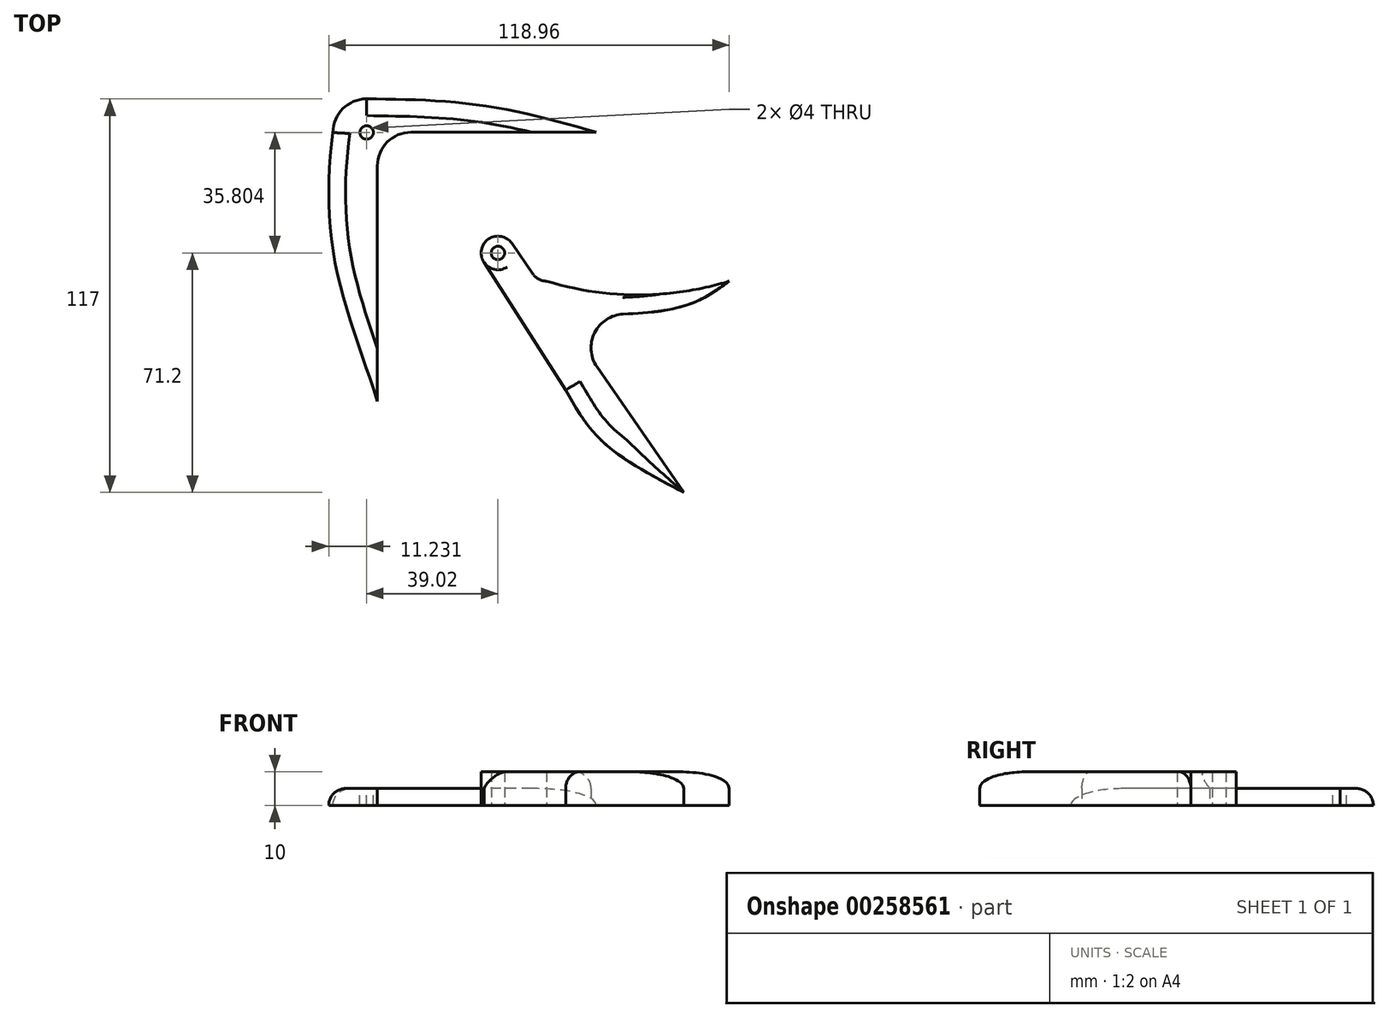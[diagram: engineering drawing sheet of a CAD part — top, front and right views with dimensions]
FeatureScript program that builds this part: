
annotation { "Feature Type Name" : "Feature", "Feature Type Description" : "" }
export const myFeature = defineFeature(function(context is Context, id is Id, definition is map)
    precondition{}
    {
        {
            var Q0;
            Q0=qCreatedBy(makeId("Top.planeOp"),FACE);
            var sketch = newSketch(context, id + "F0", { "sketchPlane" : qUnion([Q0])});
            skLineSegment(sketch, "E0", {"start": v(30.76, 64.9) * mm, "end": v(-24.24, 64.9) * mm});
            skLineSegment(sketch, "E1", {"start": v(-34.24, 54.9) * mm, "end": v(-34.24, -15.1) * mm});
            skPoint(sketch, "E2.visualSharp", {"position": v(-46.55, 74.88) * mm});
            skArc(sketch, "E2.filletArc", {"start": v(-37.45, 74.81) * mm, "mid": v(-44.52, 71.89) * mm, "end": v(-47.45, 64.81) * mm});
            skPoint(sketch, "E3.visualSharp", {"position": v(-34.24, 64.9) * mm});
            skArc(sketch, "E3.filletArc", {"start": v(-24.24, 64.9) * mm, "mid": v(-31.3, 61.96) * mm, "end": v(-34.24, 54.9) * mm});
            skPoint(sketch, "E4.1.internal.snap0", {"position": v(-4.05, 74.88) * mm});
            skFitSpline(sketch, "E4", {"points": [v(-37.45, 74.81) * mm, v(-4.05, 72.97) * mm, v(30.76, 64.9) * mm], "startDerivative": vector(65.7, -0.83) * mm, "endDerivative": vector(64.31, -19.13) * mm});
            skFitSpline(sketch, "E5", {"points": [v(-47.45, 64.81) * mm, v(-46.55, 24.86) * mm, v(-34.24, -15.1) * mm], "startDerivative": vector(-10.85, -80.35) * mm, "endDerivative": vector(24.85, -79.1) * mm});
            skSolve(sketch);
        }
        {
            var Q0;
            Q0=makeQuery(id+"F0.imprint","IMPRINT",FACE,{"disambiguationData":[TD([[makeQuery(id+"F0.imprint","IMPRINT",EDGE,{"derivedFrom":sQuery(id+"F0.wireOp",EDGE,"E0")}),-1.0]])]});
            extrude(context, id + "F1", {"entities" : qUnion([Q0]), "depth" : 5 * mm});
        }
        {
            var Q0;
            Q0=makeQuery(id+"F1.opExtrude","CAP_EDGE",EDGE,{"disambiguationData":[OSD([sQuery(id+"F0.wireOp",EDGE,"E5")])],"isStart":false});
            var Q1;
            Q1=makeQuery(id+"F1.opExtrude","CAP_EDGE",EDGE,{"disambiguationData":[OSD([sQuery(id+"F0.wireOp",EDGE,"E4")])],"isStart":false});
            var Q2;
            Q2=makeQuery(id+"F1.opExtrude","CAP_EDGE",EDGE,{"disambiguationData":[OSD([sQuery(id+"F0.wireOp",EDGE,"E2.filletArc")])],"isStart":false});
            fillet(context, id + "F2", {"entities" : qUnion([Q0, Q1, Q2]), "radius" : 5 * mm, "tangentPropagation" : true, "allowEdgeOverflow" : false});
        }
        {
            var Q0;
            Q0=qCreatedBy(makeId("Top.planeOp"),FACE);
            var sketch = newSketch(context, id + "F3", { "sketchPlane" : qUnion([Q0])});
            skArc(sketch, "E6", {"start": v(5.7, 31.84) * mm, "mid": v(-1.26, 33.13) * mm, "end": v(-2.55, 26.18) * mm});
            skLineSegment(sketch, "E7", {"start": v(-2.55, 26.18) * mm, "end": v(21.67, -11.75) * mm});
            skFitSpline(sketch, "E8", {"points": [v(20.28, 10.63) * mm, v(56.46, 13.13) * mm, v(70.28, 20.63) * mm], "startDerivative": vector(67.6, -0.3) * mm, "endDerivative": vector(29.8, 21.82) * mm});
            skLineSegment(sketch, "E9", {"start": v(5.7, 31.84) * mm, "end": v(11.91, 22.8) * mm});
            skLineSegment(sketch, "E10", {"start": v(30.98, -4.86) * mm, "end": v(56.77, -42.19) * mm});
            skFitSpline(sketch, "E11", {"points": [v(21.67, -11.75) * mm, v(32.7, -27.13) * mm, v(56.77, -42.19) * mm], "startDerivative": vector(20.27, -35.71) * mm, "endDerivative": vector(48.82, -25.74) * mm});
            skArc(sketch, "E12.filletArc", {"start": v(38.8, 10.82) * mm, "mid": v(30.26, 5.29) * mm, "end": v(30.98, -4.86) * mm});
            skPoint(sketch, "E13.visualSharp", {"position": v(13.4, 20.63) * mm});
            skArc(sketch, "E13.filletArc", {"start": v(11.91, 22.8) * mm, "mid": v(13.7, 21.2) * mm, "end": v(16.03, 20.63) * mm});
            skArc(sketch, "E14", {"start": v(16.03, 20.63) * mm, "mid": v(43.16, 16.55) * mm, "end": v(70.28, 20.63) * mm});
            skCircle(sketch, "E15", {"center": v(1.57, 29.01) * mm, "radius": 2 * mm});
            skSolve(sketch);
        }
        {
            var Q0;
            Q0=makeQuery(id+"F3.imprint","IMPRINT",FACE,{"disambiguationData":[TD([[makeQuery(id+"F3.imprint","IMPRINT",EDGE,{"derivedFrom":sQuery(id+"F3.wireOp",EDGE,"E6")}),1.0]])]});
            extrude(context, id + "F4", {"entities" : qUnion([Q0]), "depth" : 10 * mm});
        }
        {
            var Q0;
            Q0=makeQuery(id+"F4.opExtrude","CAP_EDGE",EDGE,{"disambiguationData":[OSD([sQuery(id+"F3.wireOp",EDGE,"E7")])],"isStart":false});
            var Q1;
            Q1=makeQuery(id+"F4.opExtrude","CAP_EDGE",EDGE,{"disambiguationData":[OSD([sQuery(id+"F3.wireOp",EDGE,"E10")])],"isStart":false});
            fillet(context, id + "F5", {"entities" : qUnion([Q0, Q1]), "radius" : 5 * mm, "tangentPropagation" : true, "allowEdgeOverflow" : false});
        }
        {
            var Q0;
            Q0=makeQuery(id+"F1.opExtrude","CAP_FACE",FACE,{"disambiguationData":[OSD([sQuery(id+"F0.wireOp",EDGE,"E0"),sQuery(id+"F0.wireOp",EDGE,"E1"),sQuery(id+"F0.wireOp",EDGE,"E2.filletArc"),sQuery(id+"F0.wireOp",EDGE,"E3.filletArc"),sQuery(id+"F0.wireOp",EDGE,"E4"),sQuery(id+"F0.wireOp",EDGE,"E5")])],"isStart":false});
            var sketch = newSketch(context, id + "F6", { "sketchPlane" : qUnion([Q0])});
            skCircle(sketch, "E16", {"center": v(-37.45, 64.81) * mm, "radius": 2 * mm});
            skSolve(sketch);
        }
        {
            var Q0;
            Q0=makeQuery(id+"F6.imprint","IMPRINT",FACE,{"disambiguationData":[TD([[makeQuery(id+"F6.imprint","IMPRINT",EDGE,{"derivedFrom":sQuery(id+"F6.wireOp",EDGE,"E16")}),1.0]])]});
            extrude(context, id + "F7", {"entities" : qUnion([Q0]), "operationType" : NewBodyOperationType.REMOVE, "endBound" : BoundingType.THROUGH_ALL, "oppositeDirection" : true, "depth" : 25 * mm});
        }
    });
